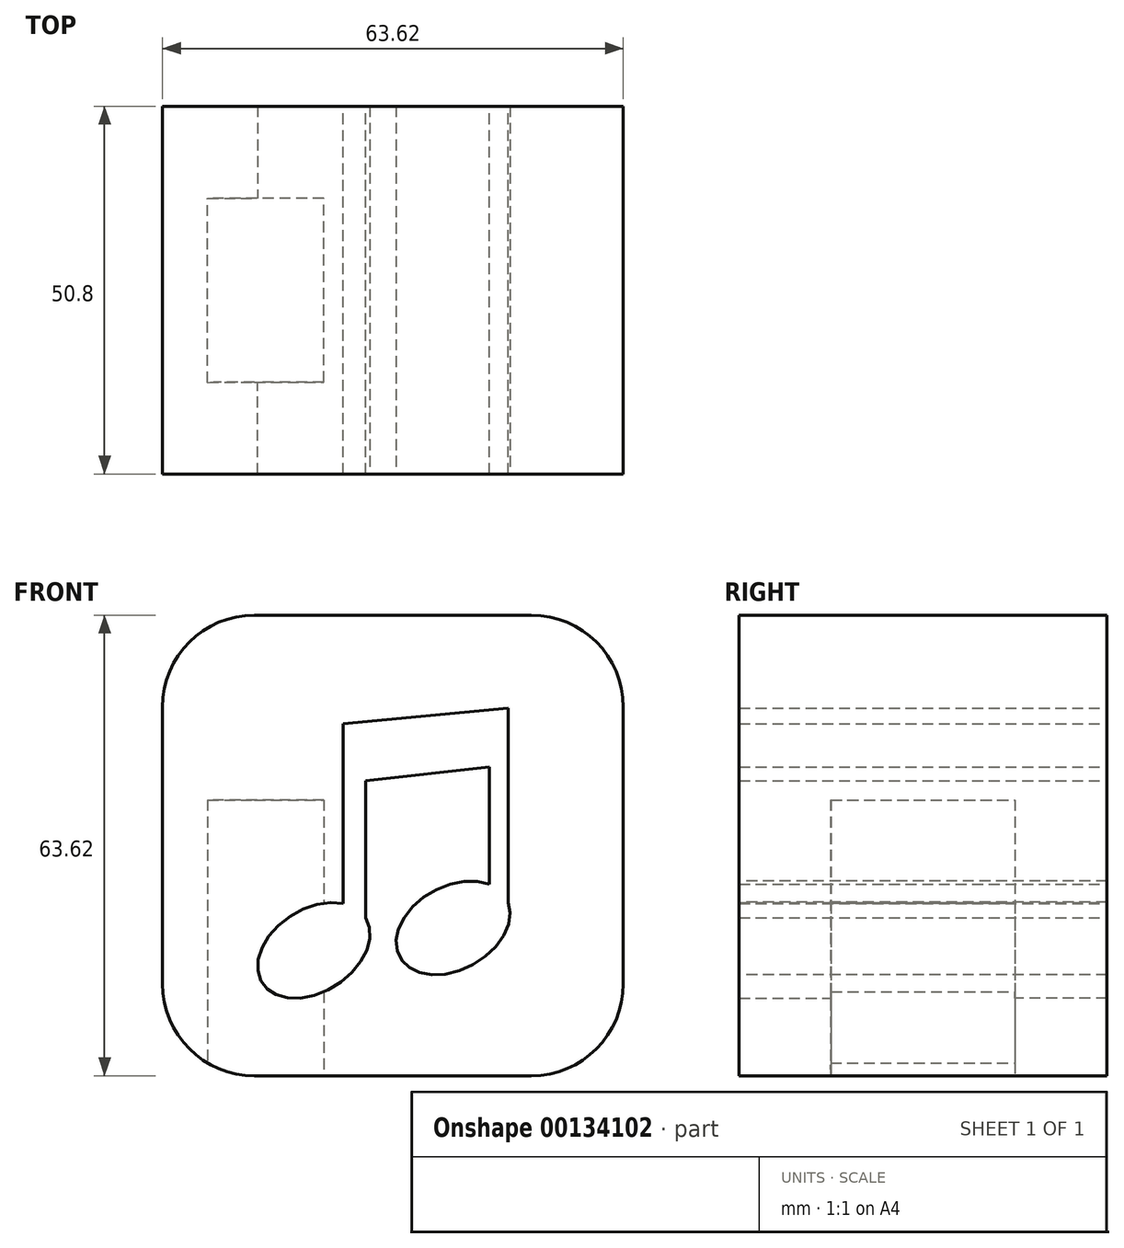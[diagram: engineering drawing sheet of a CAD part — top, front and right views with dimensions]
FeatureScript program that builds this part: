
annotation { "Feature Type Name" : "Feature", "Feature Type Description" : "" }
export const myFeature = defineFeature(function(context is Context, id is Id, definition is map)
    precondition{}
    {
        {
            var Q0;
            Q0=qCreatedBy(makeId("Front.planeOp"),FACE);
            var sketch = newSketch(context, id + "F0", { "sketchPlane" : qUnion([Q0])});
            skLineSegment(sketch, "E0.bottom", {"start": v(19.11, 31.81) * mm, "end": v(-19.11, 31.81) * mm});
            skLineSegment(sketch, "E0.top", {"start": v(19.11, -31.81) * mm, "end": v(-19.11, -31.81) * mm});
            skLineSegment(sketch, "E0.left", {"start": v(31.81, 19.11) * mm, "end": v(31.81, -19.11) * mm});
            skLineSegment(sketch, "E0.right", {"start": v(-31.81, 19.11) * mm, "end": v(-31.81, -19.11) * mm});
            skPoint(sketch, "E0.middle", {"position": v(0, 0) * mm});
            skPoint(sketch, "E1.visualSharp", {"position": v(-31.81, 31.81) * mm});
            skArc(sketch, "E1.filletArc", {"start": v(-19.11, 31.81) * mm, "mid": v(-28.1, 28.1) * mm, "end": v(-31.81, 19.11) * mm});
            skPoint(sketch, "E2.visualSharp", {"position": v(31.81, 31.81) * mm});
            skArc(sketch, "E2.filletArc", {"start": v(31.81, 19.11) * mm, "mid": v(28.1, 28.1) * mm, "end": v(19.11, 31.81) * mm});
            skPoint(sketch, "E3.visualSharp", {"position": v(31.81, -31.81) * mm});
            skArc(sketch, "E3.filletArc", {"start": v(19.11, -31.81) * mm, "mid": v(28.1, -28.1) * mm, "end": v(31.81, -19.11) * mm});
            skPoint(sketch, "E4.visualSharp", {"position": v(-31.81, -31.81) * mm});
            skArc(sketch, "E4.filletArc", {"start": v(-31.81, -19.11) * mm, "mid": v(-28.1, -28.1) * mm, "end": v(-19.11, -31.81) * mm});
            skLineSegment(sketch, "E5", {"start": v(15.9, 19) * mm, "end": v(15.9, -11.07) * mm});
            skEllipticalArc(sketch, "E6", {});
            skLineSegment(sketch, "E7", {"start": v(-6.88, 16.78) * mm, "end": v(15.9, 19) * mm});
            skLineSegment(sketch, "E8", {"start": v(13.3, 10.87) * mm, "end": v(-3.8, 8.95) * mm});
            skLineSegment(sketch, "E9", {"start": v(-3.8, 8.95) * mm, "end": v(-3.8, -14) * mm});
            skLineSegment(sketch, "E10", {"start": v(-6.88, 16.78) * mm, "end": v(-6.88, -9.26) * mm});
            skLineSegment(sketch, "E11", {"start": v(13.3, 10.87) * mm, "end": v(13.3, -5.37) * mm});
            skLineSegment(sketch, "E12.trimOffspring", {"start": v(0, 17.45) * mm, "end": v(0, 19) * mm});
            skEllipticalArc(sketch, "E13", {});
            const initialGuessF0  = {"E6": [0.008309643715620041, -0.011396083980798721, 0.8768123664212224, 0.48083268825113795, 0.008394008390911077, 0.005772837496460954, 0.5226413768355559, 6.184625316490779], "E13": [-0.010921246372163296, -0.014482522383332253, 0.844819088869705, 0.5350520601599077, 0.008430860661384052, 0.0057392072862131405, 0.6153833843198846, 6.280690361393935]};
            skSetInitialGuess(sketch, initialGuessF0);
            skSolve(sketch);
        }
        {
            var Q0;
            Q0 = qSketchRegion(id + "F0", true);
            extrude(context, id + "F1", {"entities" : qUnion([Q0]), "depth" : 50.8 * mm});
        }
        {
            var Q0;
            Q0=makeQuery(id+"F1.opExtrude","SWEPT_FACE",FACE,{"disambiguationData":[OSD([sQuery(id+"F0.wireOp",EDGE,"E0.top")])]});
            var sketch = newSketch(context, id + "F2", { "sketchPlane" : qUnion([Q0])});
            skLineSegment(sketch, "E14", {"start": v(-9.56, 12.7) * mm, "end": v(-19.11, 12.7) * mm});
            skLineSegment(sketch, "E15", {"start": v(-19.11, 38.1) * mm, "end": v(-9.56, 38.1) * mm});
            skLineSegment(sketch, "E16", {"start": v(-9.56, 38.1) * mm, "end": v(-9.56, 12.7) * mm});
            skLineSegment(sketch, "E17", {"start": v(-19.11, 12.7) * mm, "end": v(-25.58, 12.7) * mm});
            skLineSegment(sketch, "E18", {"start": v(-25.58, 38.16) * mm, "end": v(-19.11, 38.1) * mm});
            skLineSegment(sketch, "E19", {"start": v(-25.58, 38.16) * mm, "end": v(-25.58, 12.7) * mm});
            skLineSegment(sketch, "E20", {"start": v(-25.58, 12.7) * mm, "end": v(-9.56, 12.7) * mm});
            skPoint(sketch, "E21.orphan", {"position": v(-32.05, 38.22) * mm});
            skPoint(sketch, "E22.orphan", {"position": v(-32.05, 12.7) * mm});
            skPoint(sketch, "E23.orphan", {"position": v(-19.11, 25.4) * mm});
            skPoint(sketch, "E24.start.orphan", {"position": v(-19.11, 0) * mm});
            skPoint(sketch, "E25.end.orphan", {"position": v(-19.11, 50.8) * mm});
            skPoint(sketch, "E26.orphan", {"position": v(0, 50.8) * mm});
            skPoint(sketch, "E27.orphan", {"position": v(0, 38.1) * mm});
            skPoint(sketch, "E28.orphan", {"position": v(0, 25.4) * mm});
            skPoint(sketch, "E29.end.orphan", {"position": v(0, 0) * mm});
            skPoint(sketch, "E30.orphan", {"position": v(0, 12.7) * mm});
            skSolve(sketch);
        }
        {
            var Q0;
            Q0 = qSketchRegion(id + "F2", true);
            var Q1;
            {var subQ0=sQuery(id+"F2.wireOp",EDGE,"E15");Q1=makeQuery(id+"F2.imprint","IMPRINT",FACE,{"disambiguationData":[TD([[makeQuery(id+"F2.imprint","IMPRINT",EDGE,{"derivedFrom":subQ0}),-1.0]])]});}
            extrude(context, id + "F3", {"entities" : qUnion([Q0, Q1]), "operationType" : NewBodyOperationType.REMOVE, "oppositeDirection" : true, "depth" : 38.1 * mm});
        }
    });
